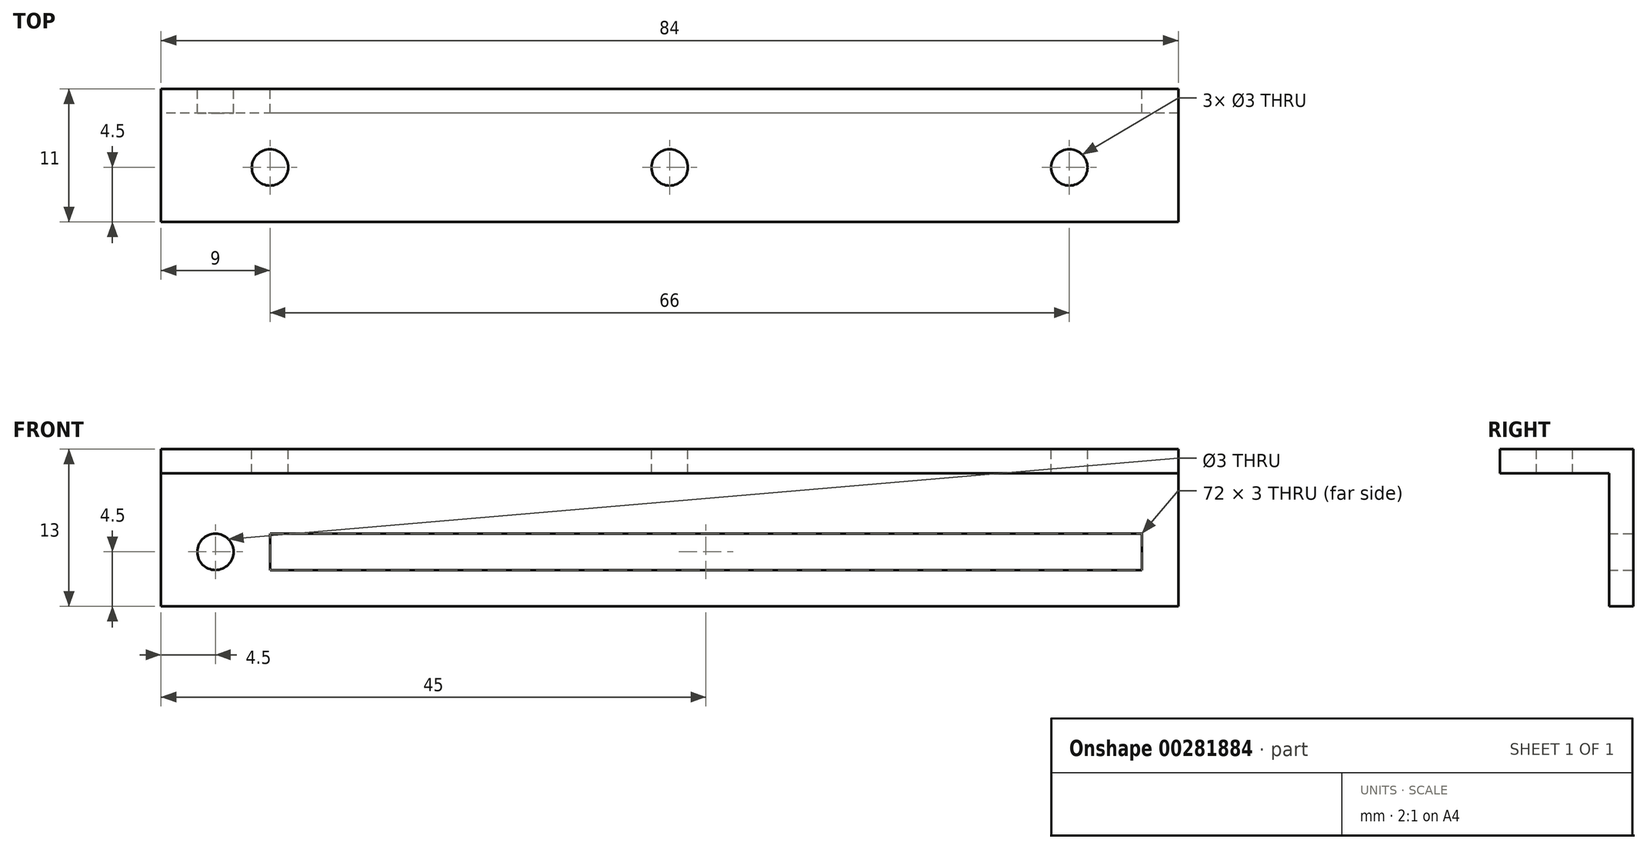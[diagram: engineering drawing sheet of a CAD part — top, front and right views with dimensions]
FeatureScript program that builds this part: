
annotation { "Feature Type Name" : "Feature", "Feature Type Description" : "" }
export const myFeature = defineFeature(function(context is Context, id is Id, definition is map)
    precondition{}
    {
        {
            var Q0;
            Q0=qCreatedBy(makeId("Front.planeOp"),FACE);
            var sketch = newSketch(context, id + "F0", { "sketchPlane" : qUnion([Q0])});
            skLineSegment(sketch, "E0.bottom", {"start": v(42, 4.5) * mm, "end": v(-42, 4.5) * mm});
            skLineSegment(sketch, "E0.top", {"start": v(42, -4.5) * mm, "end": v(-42, -4.5) * mm});
            skLineSegment(sketch, "E0.left", {"start": v(42, 4.5) * mm, "end": v(42, -4.5) * mm});
            skLineSegment(sketch, "E0.right", {"start": v(-42, 4.5) * mm, "end": v(-42, -4.5) * mm});
            skPoint(sketch, "E0.middle", {"position": v(0, 0) * mm});
            skLineSegment(sketch, "E1.bottom", {"start": v(39, 1.5) * mm, "end": v(-33, 1.5) * mm});
            skLineSegment(sketch, "E1.top", {"start": v(39, -1.5) * mm, "end": v(-33, -1.5) * mm});
            skLineSegment(sketch, "E1.left", {"start": v(39, 1.5) * mm, "end": v(39, -1.5) * mm});
            skLineSegment(sketch, "E1.right", {"start": v(-33, 1.5) * mm, "end": v(-33, -1.5) * mm});
            skCircle(sketch, "E2", {"center": v(-37.5, 0) * mm, "radius": 1.5 * mm});
            skLineSegment(sketch, "E3.top", {"start": v(42, 8.5) * mm, "end": v(-42, 8.5) * mm});
            skLineSegment(sketch, "E3.left", {"start": v(42, 4.5) * mm, "end": v(42, 8.5) * mm});
            skLineSegment(sketch, "E3.right", {"start": v(-42, 4.5) * mm, "end": v(-42, 8.5) * mm});
            skSolve(sketch);
        }
        {
            var Q0;
            Q0=qSketchRegion(id+"F0",true);
            extrude(context, id + "F1", {"entities" : qUnion([Q0]), "depth" : 2 * mm});
        }
        {
            var Q0;
            Q0=makeQuery(id+"F1.opExtrude","CAP_FACE",FACE,{"disambiguationData":[OSD([sQuery(id+"F0.wireOp",EDGE,"E0.top"),sQuery(id+"F0.wireOp",EDGE,"E0.left"),sQuery(id+"F0.wireOp",EDGE,"E0.right"),sQuery(id+"F0.wireOp",EDGE,"E1.bottom"),sQuery(id+"F0.wireOp",EDGE,"E1.top"),sQuery(id+"F0.wireOp",EDGE,"E1.left"),sQuery(id+"F0.wireOp",EDGE,"E1.right"),sQuery(id+"F0.wireOp",EDGE,"E2"),sQuery(id+"F0.wireOp",EDGE,"E3.top"),sQuery(id+"F0.wireOp",EDGE,"E3.left"),sQuery(id+"F0.wireOp",EDGE,"E3.right")])],"isStart":false});
            var sketch = newSketch(context, id + "F2", { "sketchPlane" : qUnion([Q0])});
            skLineSegment(sketch, "E4.bottom", {"start": v(42, 8.5) * mm, "end": v(-42, 8.5) * mm});
            skLineSegment(sketch, "E4.top", {"start": v(42, 6.5) * mm, "end": v(-42, 6.5) * mm});
            skLineSegment(sketch, "E4.left", {"start": v(42, 8.5) * mm, "end": v(42, 6.5) * mm});
            skLineSegment(sketch, "E4.right", {"start": v(-42, 8.5) * mm, "end": v(-42, 6.5) * mm});
            skSolve(sketch);
        }
        {
            var Q0;
            Q0=qSketchRegion(id+"F2",true);
            extrude(context, id + "F3", {"entities" : qUnion([Q0]), "operationType" : NewBodyOperationType.ADD, "depth" : 9 * mm});
        }
        {
            var Q0;
            Q0=makeQuery(id+"F3.boolean.opBoolean","MERGE",FACE,{"derivedFrom":[makeQuery(id+"F1.opExtrude","SWEPT_FACE",FACE,{"disambiguationData":[OSD([sQuery(id+"F0.wireOp",EDGE,"E3.top")])]}),makeQuery(id+"F3.opExtrude","SWEPT_FACE",FACE,{"disambiguationData":[OSD([sQuery(id+"F2.wireOp",EDGE,"E4.bottom")])]})]});
            var sketch = newSketch(context, id + "F4", { "sketchPlane" : qUnion([Q0])});
            skCircle(sketch, "E5", {"center": v(0, -6.5) * mm, "radius": 1.5 * mm});
            skCircle(sketch, "E6", {"center": v(33, -6.5) * mm, "radius": 1.5 * mm});
            skCircle(sketch, "E7", {"center": v(-33, -6.5) * mm, "radius": 1.5 * mm});
            skSolve(sketch);
        }
        {
            var Q0;
            Q0=qSketchRegion(id+"F4",true);
            extrude(context, id + "F5", {"entities" : qUnion([Q0]), "operationType" : NewBodyOperationType.REMOVE, "oppositeDirection" : true, "depth" : 25 * mm});
        }
    });
